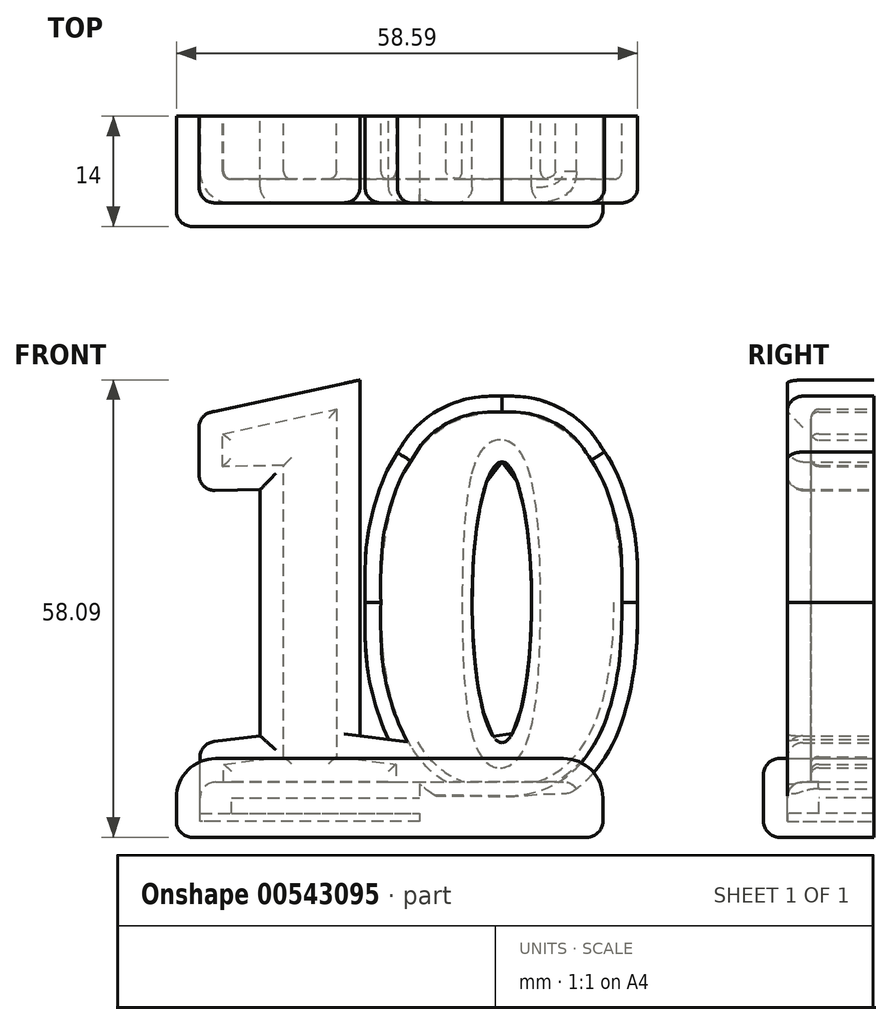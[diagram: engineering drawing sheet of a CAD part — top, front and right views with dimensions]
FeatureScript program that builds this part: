
annotation { "Feature Type Name" : "Feature", "Feature Type Description" : "" }
export const myFeature = defineFeature(function(context is Context, id is Id, definition is map)
    precondition{}
    {
        {
            assignVariable(context, id + "F0", {"name" : "wall", "anyValue" : 3});
        }
        {
            assignVariable(context, id + "F1", {"name" : "depth", "anyValue" : 8});
        }
        {
            assignVariable(context, id + "F2", {"name" : "base", "anyValue" : 4});
        }
        {
            var Q0;
            Q0=qCreatedBy(makeId("Front.planeOp"),FACE);
            var sketch = newSketch(context, id + "F3", { "sketchPlane" : qUnion([Q0])});
            skText(sketch, "E0", { "text": "1", "fontName": "RobotoSlab-Regular.ttf"});
            skText(sketch, "E1", { "text": "0", "fontName": "Tinos-Bold.ttf"});
            const initialGuessF3  = {"E0": [0, 0, 1, 0, 0.05], "E1": [0.02132, 0.001, 1, 0, 0.052]};
            skSetInitialGuess(sketch, initialGuessF3);
            skSolve(sketch);
        }
        {
            var Q0;
            Q0 = qSketchRegion(id + "F3", true);
            extrude(context, id + "F4", {"entities" : qUnion([Q0]), "depth" : (getVariable(context, 'depth')) * mm, "offsetDistance" : 25 * mm});
        }
        {
            var Q0;
            Q0=makeQuery(id+"F4.opExtrude","CAP_EDGE",EDGE,{"disambiguationData":[OSD([sQuery(id+"F3.wireOp",EDGE,"E0.sketch_text.stroke-4")])],"isStart":false});
            var Q1;
            Q1=makeQuery(id+"F4.opExtrude","CAP_EDGE",EDGE,{"disambiguationData":[OSD([sQuery(id+"F3.wireOp",EDGE,"E0.sketch_text.stroke-5")])],"isStart":false});
            var Q2;
            Q2=makeQuery(id+"F4.opExtrude","CAP_EDGE",EDGE,{"disambiguationData":[OSD([sQuery(id+"F3.wireOp",EDGE,"E0.sketch_text.stroke-6")])],"isStart":false});
            var Q3;
            Q3=makeQuery(id+"F4.opExtrude","CAP_EDGE",EDGE,{"disambiguationData":[OSD([sQuery(id+"F3.wireOp",EDGE,"E0.sketch_text.stroke-7")])],"isStart":false});
            var Q4;
            Q4=makeQuery(id+"F4.opExtrude","CAP_EDGE",EDGE,{"disambiguationData":[OSD([sQuery(id+"F3.wireOp",EDGE,"E0.sketch_text.stroke-8")])],"isStart":false});
            var Q5;
            Q5=makeQuery(id+"F4.opExtrude","CAP_EDGE",EDGE,{"disambiguationData":[OSD([sQuery(id+"F3.wireOp",EDGE,"E0.sketch_text.stroke-9")])],"isStart":false});
            var Q6;
            Q6=makeQuery(id+"F4.opExtrude","CAP_EDGE",EDGE,{"disambiguationData":[OSD([sQuery(id+"F3.wireOp",EDGE,"E0.sketch_text.stroke-1")])],"isStart":false});
            var Q7;
            Q7=makeQuery(id+"F4.opExtrude","CAP_EDGE",EDGE,{"disambiguationData":[OSD([sQuery(id+"F3.wireOp",EDGE,"E0.sketch_text.stroke-2")])],"isStart":false});
            var Q8;
            Q8=makeQuery(id+"F4.opExtrude","CAP_EDGE",EDGE,{"disambiguationData":[OSD([sQuery(id+"F3.wireOp",EDGE,"E0.sketch_text.stroke-3")])],"isStart":false});
            var Q9;
            Q9=makeQuery(id+"F4.opExtrude","CAP_EDGE",EDGE,{"disambiguationData":[OSD([sQuery(id+"F3.wireOp",EDGE,"E0.sketch_text.stroke-0")])],"isStart":false});
            fillet(context, id + "F5", {"entities" : qUnion([Q0, Q1, Q2, Q3, Q4, Q5, Q6, Q7, Q8, Q9]), "radius" : 1 * mm, "tangentPropagation" : true, "allowEdgeOverflow" : false});
        }
        {
            var Q0;
            Q0=makeQuery(id+"F4.opExtrude","CAP_EDGE",EDGE,{"disambiguationData":[OSD([sQuery(id+"F3.wireOp",EDGE,"E1.sketch_text.stroke-5")])],"isStart":false});
            var Q1;
            Q1=makeQuery(id+"F4.opExtrude","CAP_FACE",FACE,{"disambiguationData":[OSD([sQuery(id+"F3.wireOp",EDGE,"E1.sketch_text.stroke-0"),sQuery(id+"F3.wireOp",EDGE,"E1.sketch_text.stroke-1"),sQuery(id+"F3.wireOp",EDGE,"E1.sketch_text.stroke-2"),sQuery(id+"F3.wireOp",EDGE,"E1.sketch_text.stroke-3"),sQuery(id+"F3.wireOp",EDGE,"E1.sketch_text.stroke-4"),sQuery(id+"F3.wireOp",EDGE,"E1.sketch_text.stroke-5"),sQuery(id+"F3.wireOp",EDGE,"E1.sketch_text.stroke-6"),sQuery(id+"F3.wireOp",EDGE,"E1.sketch_text.stroke-7"),sQuery(id+"F3.wireOp",EDGE,"E1.sketch_text.stroke-8"),sQuery(id+"F3.wireOp",EDGE,"E1.sketch_text.stroke-9"),sQuery(id+"F3.wireOp",EDGE,"E1.sketch_text.stroke-10"),sQuery(id+"F3.wireOp",EDGE,"E1.sketch_text.stroke-11"),sQuery(id+"F3.wireOp",EDGE,"E1.sketch_text.stroke-12"),sQuery(id+"F3.wireOp",EDGE,"E1.sketch_text.stroke-13"),sQuery(id+"F3.wireOp",EDGE,"E1.sketch_text.stroke-14")])],"isStart":false});
            fillet(context, id + "F6", {"entities" : qUnion([Q0, Q1]), "radius" : 1 * mm, "tangentPropagation" : true, "allowEdgeOverflow" : false});
        }
        {
            var Q0;
            Q0=qCreatedBy(makeId("Top.planeOp"),FACE);
            cPlane(context, id + "F7", {"entities" : qUnion([Q0]), "cplaneType" : CPlaneType.OFFSET, "offset" : (getVariable(context, 'base') / 2) * mm, "width" : 150 * mm, "height" : 150 * mm});
        }
        {
            var Q0;
            Q0=qCreatedBy(id+"F7.planeOp",FACE);
            var sketch = newSketch(context, id + "F8", { "sketchPlane" : qUnion([Q0])});
            skLineSegment(sketch, "E2", {"start": v(46.27, -7) * mm, "end": v(46.27, 0) * mm});
            skLineSegment(sketch, "E3", {"start": v(32.36, 0) * mm, "end": v(32.36, -7) * mm});
            skLineSegment(sketch, "E4", {"start": v(32.36, 0) * mm, "end": v(46.27, 0) * mm});
            skLineSegment(sketch, "E5", {"start": v(4.1, 0) * mm, "end": v(26, 0) * mm});
            skLineSegment(sketch, "E6", {"start": v(4.1, 0) * mm, "end": v(4.1, -7) * mm});
            skLineSegment(sketch, "E7", {"start": v(5.1, -8) * mm, "end": v(25, -8) * mm});
            skLineSegment(sketch, "E8", {"start": v(34.71, -8) * mm, "end": v(43.83, -8) * mm});
            skFitSpline(sketch, "E9", {"points": [v(32.36, -7) * mm, v(32.36, -7.12) * mm, v(32.44, -7.34) * mm, v(32.7, -7.58) * mm, v(33.01, -7.74) * mm, v(33.45, -7.9) * mm, v(34.02, -7.98) * mm, v(34.48, -8) * mm, v(34.71, -8) * mm]});
            skFitSpline(sketch, "E10", {"points": [v(43.83, -8) * mm, v(44.07, -8) * mm, v(44.42, -7.99) * mm, v(44.89, -7.93) * mm, v(45.24, -7.86) * mm, v(45.58, -7.75) * mm, v(45.9, -7.59) * mm, v(46.17, -7.35) * mm, v(46.27, -7.12) * mm, v(46.27, -7) * mm]});
            skArc(sketch, "E11", {"start": v(4.1, -7) * mm, "mid": v(4.4, -7.7) * mm, "end": v(5.1, -8) * mm});
            skArc(sketch, "E12", {"start": v(25, -8) * mm, "mid": v(25.72, -7.7) * mm, "end": v(26, -7) * mm});
            skLineSegment(sketch, "E13", {"start": v(26, -7) * mm, "end": v(26, 0) * mm});
            skLineSegment(sketch, "E14.0", {"start": v(1.1, 3) * mm, "end": v(1.1, -7) * mm});
            skLineSegment(sketch, "E14.1", {"start": v(29, -7) * mm, "end": v(29, 3) * mm});
            skArc(sketch, "E14.2", {"start": v(25, -11) * mm, "mid": v(27.84, -9.83) * mm, "end": v(29, -7) * mm});
            skLineSegment(sketch, "E14.3", {"start": v(1.1, 3) * mm, "end": v(29, 3) * mm});
            skLineSegment(sketch, "E14.4", {"start": v(5.1, -11) * mm, "end": v(25, -11) * mm});
            skArc(sketch, "E14.5", {"start": v(1.1, -7) * mm, "mid": v(2.27, -9.83) * mm, "end": v(5.1, -11) * mm});
            skLineSegment(sketch, "E15.0", {"start": v(29.36, 3) * mm, "end": v(29.36, -7) * mm});
            skLineSegment(sketch, "E15.1", {"start": v(49.27, -7) * mm, "end": v(49.27, 3) * mm});
            skFitSpline(sketch, "E15.2", {"points": [v(43.83, -11) * mm, v(43.98, -11) * mm, v(44.3, -11) * mm, v(44.81, -10.96) * mm, v(45.37, -10.9) * mm, v(45.88, -10.79) * mm, v(46.34, -10.66) * mm, v(46.64, -10.55) * mm, v(46.9, -10.43) * mm, v(47.11, -10.33) * mm, v(47.33, -10.22) * mm, v(47.55, -10.08) * mm, v(47.78, -9.91) * mm, v(48.04, -9.7) * mm, v(48.31, -9.43) * mm, v(48.59, -9.1) * mm, v(48.84, -8.7) * mm, v(49.06, -8.22) * mm, v(49.22, -7.66) * mm, v(49.27, -7.23) * mm, v(49.27, -7) * mm]});
            skLineSegment(sketch, "E15.3", {"start": v(29.36, 3) * mm, "end": v(49.27, 3) * mm});
            skLineSegment(sketch, "E15.4", {"start": v(34.71, -11) * mm, "end": v(43.83, -11) * mm});
            skFitSpline(sketch, "E15.5", {"points": [v(29.36, -7) * mm, v(29.36, -7.21) * mm, v(29.4, -7.62) * mm, v(29.54, -8.16) * mm, v(29.74, -8.63) * mm, v(29.98, -9.03) * mm, v(30.25, -9.36) * mm, v(30.5, -9.64) * mm, v(30.76, -9.86) * mm, v(31, -10.03) * mm, v(31.22, -10.18) * mm, v(31.43, -10.3) * mm, v(31.64, -10.4) * mm, v(31.9, -10.52) * mm, v(32.21, -10.64) * mm, v(32.55, -10.74) * mm, v(32.86, -10.82) * mm, v(33.17, -10.88) * mm, v(33.46, -10.92) * mm, v(33.73, -10.95) * mm, v(33.98, -10.98) * mm, v(34.32, -11) * mm, v(34.56, -11) * mm, v(34.71, -11) * mm]});
            skLineSegment(sketch, "E16", {"start": v(29, 3) * mm, "end": v(29.36, 3) * mm});
            skLineSegment(sketch, "E17", {"start": v(34.71, -11) * mm, "end": v(25, -11) * mm});
            skLineSegment(sketch, "E18", {"start": v(26, 0) * mm, "end": v(32.36, 0) * mm});
            skLineSegment(sketch, "E19", {"start": v(46.27, 0) * mm, "end": v(49.27, 0) * mm});
            skLineSegment(sketch, "E20", {"start": v(4.1, 0) * mm, "end": v(1.1, 0) * mm});
            skSolve(sketch);
        }
        {
            var Q0;
            Q0=makeQuery(id+"F8.imprint","IMPRINT",FACE,{"disambiguationData":[TD([[makeQuery(id+"F8.imprint","IMPRINT",EDGE,{"derivedFrom":sQuery(id+"F8.wireOp",EDGE,"E6")}),-1.0]])]});
            var Q1;
            Q1=makeQuery(id+"F8.imprint","IMPRINT",FACE,{"disambiguationData":[TD([[makeQuery(id+"F8.imprint","IMPRINT",EDGE,{"derivedFrom":sQuery(id+"F8.wireOp",EDGE,"E5")}),-1.0]])]});
            var Q2;
            {var subQ1=sQuery(id+"F8.wireOp",EDGE,"E14.2");Q2=makeQuery(id+"F8.imprint","IMPRINT",FACE,{"disambiguationData":[TD([[makeQuery(id+"F8.imprint","IMPRINT",EDGE,{"derivedFrom":subQ1}),-1.0]])]});}
            var Q3;
            Q3=makeQuery(id+"F8.imprint","IMPRINT",FACE,{"disambiguationData":[TD([[makeQuery(id+"F8.imprint","IMPRINT",EDGE,{"derivedFrom":sQuery(id+"F8.wireOp",EDGE,"E2")}),-1.0]])]});
            var Q4;
            Q4=makeQuery(id+"F8.imprint","IMPRINT",FACE,{"disambiguationData":[TD([[makeQuery(id+"F8.imprint","IMPRINT",EDGE,{"derivedFrom":sQuery(id+"F8.wireOp",EDGE,"E2")}),1.0]])]});
            extrude(context, id + "F9", {"entities" : qUnion([Q0, Q1, Q2, Q3, Q4]), "oppositeDirection" : true, "depth" : (getVariable(context, 'base')) * mm, "offsetDistance" : 25 * mm});
        }
        {
            var Q0;
            Q0=makeQuery(id+"F9.opExtrude","CAP_EDGE",EDGE,{"disambiguationData":[OSD([sQuery(id+"F8.wireOp",EDGE,"E14.0")])],"isStart":true});
            fillet(context, id + "F10", {"entities" : qUnion([Q0]), "radius" : 2 * mm, "tangentPropagation" : true, "allowEdgeOverflow" : false});
        }
        {
            var Q0;
            Q0=qCreatedBy(makeId("Front.planeOp"),FACE);
            var sketch = newSketch(context, id + "F11", { "sketchPlane" : qUnion([Q0])});
            skFitSpline(sketch, "E21.0", {"points": [v(39.44, 51.03) * mm, v(40.82, 51.03) * mm, v(43.48, 50.74) * mm, v(47.06, 49.4) * mm, v(50.12, 47.14) * mm, v(51.77, 45.1) * mm, v(52.5, 43.94) * mm]});
            skFitSpline(sketch, "E21.1", {"points": [v(26.17, 43.85) * mm, v(26.89, 45.01) * mm, v(28.53, 47.1) * mm, v(31.63, 49.39) * mm, v(35.3, 50.74) * mm, v(38.01, 51.03) * mm, v(39.44, 51.03) * mm]});
            skFitSpline(sketch, "E21.2", {"points": [v(56.67, 24.84) * mm, v(56.67, 22.75) * mm, v(56.5, 18.8) * mm, v(55.75, 13.57) * mm, v(54.46, 9.06) * mm, v(52.6, 5.24) * mm, v(50.1, 2.15) * mm, v(46.97, -0.1) * mm, v(43.3, -1.43) * mm, v(40.58, -1.71) * mm, v(39.16, -1.71) * mm]});
            skFitSpline(sketch, "E21.3", {"points": [v(39.16, -1.71) * mm, v(37.77, -1.71) * mm, v(35.12, -1.42) * mm, v(31.54, -0.04) * mm, v(28.5, 2.27) * mm, v(26.88, 4.36) * mm, v(26.17, 5.53) * mm]});
            skFitSpline(sketch, "E21.4", {"points": [v(26.17, 5.53) * mm, v(25.46, 6.7) * mm, v(24.24, 9.26) * mm, v(22.56, 15.26) * mm, v(22.07, 20.74) * mm, v(22.07, 24.84) * mm]});
            skFitSpline(sketch, "E21.5", {"points": [v(52.5, 43.94) * mm, v(53.21, 42.8) * mm, v(54.46, 40.27) * mm, v(56.18, 34.34) * mm, v(56.67, 28.91) * mm, v(56.67, 24.84) * mm]});
            skFitSpline(sketch, "E21.6", {"points": [v(22.07, 24.84) * mm, v(22.07, 28.86) * mm, v(22.56, 34.24) * mm, v(24.25, 40.16) * mm, v(25.47, 42.7) * mm, v(26.17, 43.85) * mm]});
            skLineSegment(sketch, "E22.0", {"start": v(29, -3) * mm, "end": v(1.1, -3) * mm});
            skLineSegment(sketch, "E22.1", {"start": v(29, 6.93) * mm, "end": v(29, -3) * mm});
            skLineSegment(sketch, "E22.2", {"start": v(1.1, -3) * mm, "end": v(1.1, 6.93) * mm});
            skLineSegment(sketch, "E22.3", {"start": v(21.41, 7.87) * mm, "end": v(29, 6.93) * mm});
            skLineSegment(sketch, "E22.4", {"start": v(21.41, 53.09) * mm, "end": v(21.41, 7.87) * mm});
            skLineSegment(sketch, "E22.5", {"start": v(0.97, 48.68) * mm, "end": v(21.41, 53.09) * mm});
            skLineSegment(sketch, "E22.6", {"start": v(1.1, 6.93) * mm, "end": v(8.73, 7.87) * mm});
            skLineSegment(sketch, "E22.7", {"start": v(8.73, 7.87) * mm, "end": v(8.73, 39.17) * mm});
            skLineSegment(sketch, "E22.8", {"start": v(8.73, 39.17) * mm, "end": v(0.97, 39.02) * mm});
            skLineSegment(sketch, "E22.9", {"start": v(0.97, 39.02) * mm, "end": v(0.97, 48.68) * mm});
            skLineSegment(sketch, "E23", {"start": v(39.16, -2.71) * mm, "end": v(29, -3) * mm});
            skEllipse(sketch, "E24", {"center": v(39.44, 24.84) * mm, "majorRadius": 17.83 * mm, "minorRadius": 3.78 * mm, "majorAxis": v(0, 1)});
            skSolve(sketch);
        }
        {
            var Q0;
            Q0=qCreatedBy(makeId("Front.planeOp"),FACE);
            var sketch = newSketch(context, id + "F12", { "sketchPlane" : qUnion([Q0])});
            skLineSegment(sketch, "E25.0", {"start": v(52.27, -5) * mm, "end": v(-1.9, -5) * mm});
            skArc(sketch, "E25.1", {"start": v(-1.9, 0) * mm, "mid": v(-0.43, 3.54) * mm, "end": v(3.1, 5) * mm});
            skLineSegment(sketch, "E25.2", {"start": v(47.27, 5) * mm, "end": v(3.1, 5) * mm});
            skLineSegment(sketch, "E25.3", {"start": v(-1.9, -5) * mm, "end": v(-1.9, 0) * mm});
            skArc(sketch, "E25.4", {"start": v(47.27, 5) * mm, "mid": v(50.8, 3.54) * mm, "end": v(52.27, 0) * mm});
            skLineSegment(sketch, "E25.5", {"start": v(52.27, -5) * mm, "end": v(52.27, 0) * mm});
            skSolve(sketch);
        }
        {
            var Q0;
            Q0=makeQuery(id+"F12.imprint","IMPRINT",FACE,{"disambiguationData":[TD([[makeQuery(id+"F12.imprint","IMPRINT",EDGE,{"derivedFrom":sQuery(id+"F12.wireOp",EDGE,"E25.0")}),-1.0]])]});
            var Q1;
            Q1=makeQuery(id+"F9.opExtrude","SWEPT_FACE",FACE,{"disambiguationData":[OSD([sQuery(id+"F8.wireOp",EDGE,"E14.4"),sQuery(id+"F8.wireOp",EDGE,"E15.4"),sQuery(id+"F8.wireOp",EDGE,"E17")])]});
            extrude(context, id + "F13", {"entities" : qUnion([Q0]), "endBound" : BoundingType.UP_TO_SURFACE, "depth" : 25 * mm, "endBoundEntityFace" : qUnion([Q1]), "hasOffset" : true, "offsetDistance" : (getVariable(context, 'wall')) * mm, "offsetOppositeDirection" : true});
        }
        {
            var Q0;
            Q0=makeQuery(id+"F11.imprint","IMPRINT",FACE,{"disambiguationData":[TD([[makeQuery(id+"F11.imprint","IMPRINT",EDGE,{"derivedFrom":sQuery(id+"F11.wireOp",EDGE,"Az2pzmcp-ratZ-nB7F-bwXG-R4mNLETn0rJH.bottom")}),1.0]])]});
            var Q1;
            Q1=makeQuery(id+"F11.imprint","IMPRINT",FACE,{"disambiguationData":[TD([[makeQuery(id+"F11.imprint","IMPRINT",EDGE,{"derivedFrom":sQuery(id+"F11.wireOp",EDGE,"E21.0")}),-1.0]])]});
            var Q2;
            {var subQ9=sQuery(id+"F11.wireOp",EDGE,"E22.0");Q2=makeQuery(id+"F11.imprint","IMPRINT",FACE,{"disambiguationData":[TD([[makeQuery(id+"F11.imprint","IMPRINT",EDGE,{"derivedFrom":subQ9}),-1.0]])]});}
            var Q3;
            {var subQ0=sQuery(id+"F11.wireOp",EDGE,"E21.4");var subQ1=sQuery(id+"F11.wireOp",EDGE,"E21.3");var subQ2=makeQuery(id+"F11.imprint","INTERSECT",VERTEX,{"derivedFrom":[subQ1,subQ0]});Q3=makeQuery(id+"F11.imprint","IMPRINT",FACE,{"disambiguationData":[TD([[makeQuery(id+"F11.imprint","IMPRINT",EDGE,{"disambiguationData":[TD([[subQ2,1.0]])],"derivedFrom":subQ1}),-1.0]])]});}
            var Q4;
            {var subQ0=sQuery(id+"F11.wireOp",EDGE,"E23");Q4=makeQuery(id+"F11.imprint","IMPRINT",FACE,{"disambiguationData":[TD([[makeQuery(id+"F11.imprint","IMPRINT",EDGE,{"derivedFrom":subQ0}),-1.0]])]});}
            var Q5;
            {var subQ0=sQuery(id+"F11.wireOp",EDGE,"E21.6");var subQ1=sQuery(id+"F11.wireOp",EDGE,"E21.4");var subQ2=makeQuery(id+"F11.imprint","INTERSECT",VERTEX,{"derivedFrom":[subQ1,subQ0]});Q5=makeQuery(id+"F11.imprint","IMPRINT",FACE,{"disambiguationData":[TD([[makeQuery(id+"F11.imprint","IMPRINT",EDGE,{"disambiguationData":[TD([[subQ2,1.0]])],"derivedFrom":subQ1}),-1.0]])]});}
            extrude(context, id + "F14", {"entities" : qUnion([Q0, Q1, Q2, Q3, Q4, Q5]), "depth" : (getVariable(context, 'depth') + getVariable(context, 'wall')) * mm, "offsetDistance" : 25 * mm});
        }
        {
            var Q0;
            Q0=makeQuery(id+"F4.opExtrude","SWEPT_BODY",BODY,{"disambiguationData":[OSD([sQuery(id+"F3.wireOp",EDGE,"E0.sketch_text.stroke-0"),sQuery(id+"F3.wireOp",EDGE,"E0.sketch_text.stroke-1"),sQuery(id+"F3.wireOp",EDGE,"E0.sketch_text.stroke-2"),sQuery(id+"F3.wireOp",EDGE,"E0.sketch_text.stroke-3"),sQuery(id+"F3.wireOp",EDGE,"E0.sketch_text.stroke-4"),sQuery(id+"F3.wireOp",EDGE,"E0.sketch_text.stroke-5"),sQuery(id+"F3.wireOp",EDGE,"E0.sketch_text.stroke-6"),sQuery(id+"F3.wireOp",EDGE,"E0.sketch_text.stroke-7"),sQuery(id+"F3.wireOp",EDGE,"E0.sketch_text.stroke-8"),sQuery(id+"F3.wireOp",EDGE,"E0.sketch_text.stroke-9")])]});
            var Q1;
            Q1=makeQuery(id+"F4.opExtrude","SWEPT_BODY",BODY,{"disambiguationData":[OSD([sQuery(id+"F3.wireOp",EDGE,"E1.sketch_text.stroke-0"),sQuery(id+"F3.wireOp",EDGE,"E1.sketch_text.stroke-1"),sQuery(id+"F3.wireOp",EDGE,"E1.sketch_text.stroke-2"),sQuery(id+"F3.wireOp",EDGE,"E1.sketch_text.stroke-3"),sQuery(id+"F3.wireOp",EDGE,"E1.sketch_text.stroke-4"),sQuery(id+"F3.wireOp",EDGE,"E1.sketch_text.stroke-5"),sQuery(id+"F3.wireOp",EDGE,"E1.sketch_text.stroke-6"),sQuery(id+"F3.wireOp",EDGE,"E1.sketch_text.stroke-7"),sQuery(id+"F3.wireOp",EDGE,"E1.sketch_text.stroke-8"),sQuery(id+"F3.wireOp",EDGE,"E1.sketch_text.stroke-9"),sQuery(id+"F3.wireOp",EDGE,"E1.sketch_text.stroke-10"),sQuery(id+"F3.wireOp",EDGE,"E1.sketch_text.stroke-11"),sQuery(id+"F3.wireOp",EDGE,"E1.sketch_text.stroke-12"),sQuery(id+"F3.wireOp",EDGE,"E1.sketch_text.stroke-13"),sQuery(id+"F3.wireOp",EDGE,"E1.sketch_text.stroke-14")])]});
            var Q2;
            Q2=makeQuery(id+"F9.opExtrude","SWEPT_BODY",BODY,{"disambiguationData":[OSD([sQuery(id+"F8.wireOp",EDGE,"E4"),sQuery(id+"F8.wireOp",EDGE,"E5"),sQuery(id+"F8.wireOp",EDGE,"E14.0"),sQuery(id+"F8.wireOp",EDGE,"E14.4"),sQuery(id+"F8.wireOp",EDGE,"E14.5"),sQuery(id+"F8.wireOp",EDGE,"E15.1"),sQuery(id+"F8.wireOp",EDGE,"E15.2"),sQuery(id+"F8.wireOp",EDGE,"E15.4"),sQuery(id+"F8.wireOp",EDGE,"E17"),sQuery(id+"F8.wireOp",EDGE,"E18"),sQuery(id+"F8.wireOp",EDGE,"E19"),sQuery(id+"F8.wireOp",EDGE,"E20")])]});
            var Q3;
            Q3=makeQuery(id+"F14.opExtrude","SWEPT_BODY",BODY,{"disambiguationData":[OSD([sQuery(id+"F11.wireOp",EDGE,"E21.0"),sQuery(id+"F11.wireOp",EDGE,"E21.1"),sQuery(id+"F11.wireOp",EDGE,"E21.2"),sQuery(id+"F11.wireOp",EDGE,"E21.4"),sQuery(id+"F11.wireOp",EDGE,"E21.5"),sQuery(id+"F11.wireOp",EDGE,"E21.6"),sQuery(id+"F11.wireOp",EDGE,"E22.0"),sQuery(id+"F11.wireOp",EDGE,"E22.2"),sQuery(id+"F11.wireOp",EDGE,"E22.3"),sQuery(id+"F11.wireOp",EDGE,"E22.4"),sQuery(id+"F11.wireOp",EDGE,"E22.5"),sQuery(id+"F11.wireOp",EDGE,"E22.6"),sQuery(id+"F11.wireOp",EDGE,"E22.7"),sQuery(id+"F11.wireOp",EDGE,"E22.8"),sQuery(id+"F11.wireOp",EDGE,"E22.9"),sQuery(id+"F11.wireOp",EDGE,"E23")])]});
            booleanBodies(context, id + "F15", {"operationType" : BooleanOperationType.SUBTRACTION, "tools" : qUnion([Q0, Q1, Q2]), "targets" : qUnion([Q3])});
        }
        {
            var Q0;
            Q0=makeQuery(id+"F14.opExtrude","CAP_EDGE",EDGE,{"disambiguationData":[OSD([sQuery(id+"F11.wireOp",EDGE,"E22.9")])],"isStart":false});
            var Q1;
            Q1=makeQuery(id+"F14.opExtrude","CAP_EDGE",EDGE,{"disambiguationData":[OSD([sQuery(id+"F11.wireOp",EDGE,"E22.8")])],"isStart":false});
            var Q2;
            Q2=makeQuery(id+"F14.opExtrude","CAP_EDGE",EDGE,{"disambiguationData":[OSD([sQuery(id+"F11.wireOp",EDGE,"E22.7")])],"isStart":false});
            var Q3;
            Q3=makeQuery(id+"F14.opExtrude","CAP_EDGE",EDGE,{"disambiguationData":[OSD([sQuery(id+"F11.wireOp",EDGE,"E22.6")])],"isStart":false});
            var Q4;
            Q4=makeQuery(id+"F14.opExtrude","CAP_EDGE",EDGE,{"disambiguationData":[OSD([sQuery(id+"F11.wireOp",EDGE,"E22.2")])],"isStart":false});
            var Q5;
            Q5=makeQuery(id+"F14.opExtrude","CAP_EDGE",EDGE,{"disambiguationData":[OSD([sQuery(id+"F11.wireOp",EDGE,"E21.2")])],"isStart":false});
            var Q6;
            Q6=makeQuery(id+"F14.opExtrude","CAP_EDGE",EDGE,{"disambiguationData":[OSD([sQuery(id+"F11.wireOp",EDGE,"E21.5")])],"isStart":false});
            var Q7;
            Q7=makeQuery(id+"F14.opExtrude","CAP_EDGE",EDGE,{"disambiguationData":[OSD([sQuery(id+"F11.wireOp",EDGE,"E21.0")])],"isStart":false});
            var Q8;
            Q8=makeQuery(id+"F14.opExtrude","CAP_EDGE",EDGE,{"disambiguationData":[OSD([sQuery(id+"F11.wireOp",EDGE,"E21.1")])],"isStart":false});
            var Q9;
            Q9=makeQuery(id+"F14.opExtrude","CAP_EDGE",EDGE,{"disambiguationData":[OSD([sQuery(id+"F11.wireOp",EDGE,"E21.6")])],"isStart":false});
            var Q10;
            {var subQ0=sQuery(id+"F11.wireOp",EDGE,"E22.4");Q10=makeQuery(id+"F14.opExtrude","CAP_EDGE",EDGE,{"disambiguationData":[OSD([subQ0]),TDD([makeQuery(id+"F11.imprint","IMPRINT",EDGE,{"disambiguationData":[TD([[makeQuery(id+"F11.imprint","INTERSECT",VERTEX,{"derivedFrom":[subQ0,sQuery(id+"F11.wireOp",EDGE,"E22.5")]}),-1.0]])],"derivedFrom":subQ0})])],"isStart":false});}
            var Q11;
            Q11=makeQuery(id+"F14.opExtrude","CAP_EDGE",EDGE,{"disambiguationData":[OSD([sQuery(id+"F11.wireOp",EDGE,"E24")])],"isStart":false});
            var Q12;
            Q12=makeQuery(id+"F13.opExtrude","CAP_EDGE",EDGE,{"disambiguationData":[OSD([sQuery(id+"F12.wireOp",EDGE,"E25.5")])],"isStart":false});
            var Q13;
            Q13=makeQuery(id+"F13.opExtrude","CAP_EDGE",EDGE,{"disambiguationData":[OSD([sQuery(id+"F12.wireOp",EDGE,"E25.4")])],"isStart":false});
            var Q14;
            Q14=makeQuery(id+"F14.opExtrude","SWEPT_EDGE",EDGE,{"disambiguationData":[OSD([sQuery(id+"F11.wireOp",EDGE,"E22.5"),sQuery(id+"F11.wireOp",EDGE,"E22.9")])]});
            var Q15;
            Q15=makeQuery(id+"F14.opExtrude","SWEPT_EDGE",EDGE,{"disambiguationData":[OSD([sQuery(id+"F11.wireOp",EDGE,"E22.8"),sQuery(id+"F11.wireOp",EDGE,"E22.9")])]});
            var Q16;
            Q16=makeQuery(id+"F14.opExtrude","SWEPT_EDGE",EDGE,{"disambiguationData":[OSD([sQuery(id+"F11.wireOp",EDGE,"E22.2"),sQuery(id+"F11.wireOp",EDGE,"E22.6")])]});
            var Q17;
            Q17=makeQuery(id+"F13.opExtrude","SWEPT_EDGE",EDGE,{"disambiguationData":[OSD([sQuery(id+"F12.wireOp",EDGE,"E25.0"),sQuery(id+"F12.wireOp",EDGE,"E25.5")])]});
            var Q18;
            Q18=makeQuery(id+"F13.opExtrude","SWEPT_EDGE",EDGE,{"disambiguationData":[OSD([sQuery(id+"F12.wireOp",EDGE,"E25.0"),sQuery(id+"F12.wireOp",EDGE,"E25.3")])]});
            var Q19;
            Q19=makeQuery(id+"F13.opExtrude","CAP_EDGE",EDGE,{"disambiguationData":[OSD([sQuery(id+"F12.wireOp",EDGE,"E25.0")])],"isStart":false});
            fillet(context, id + "F16", {"entities" : qUnion([Q0, Q1, Q2, Q3, Q4, Q5, Q6, Q7, Q8, Q9, Q10, Q11, Q12, Q13, Q14, Q15, Q16, Q17, Q18, Q19]), "radius" : 2 * mm, "tangentPropagation" : true, "allowEdgeOverflow" : false});
        }
    });
